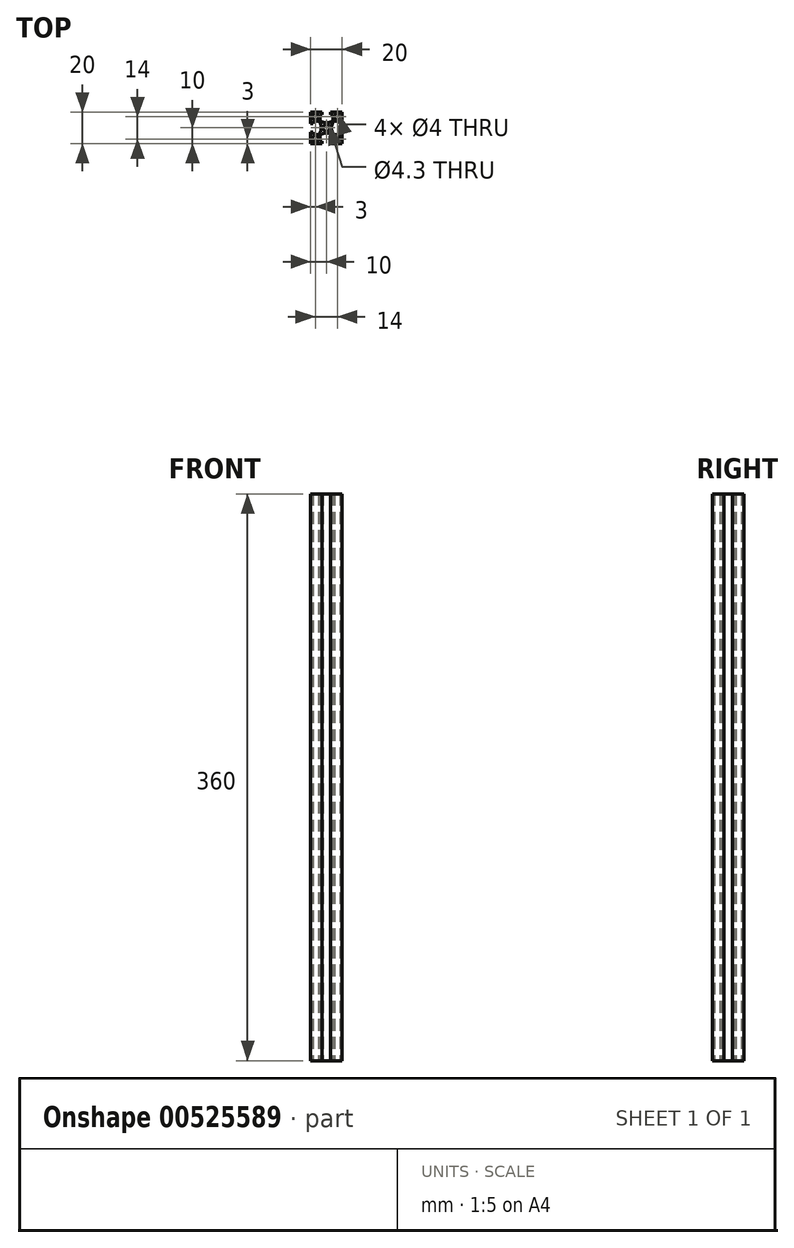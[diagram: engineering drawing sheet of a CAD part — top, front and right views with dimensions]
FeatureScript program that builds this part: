
annotation { "Feature Type Name" : "Feature", "Feature Type Description" : "" }
export const myFeature = defineFeature(function(context is Context, id is Id, definition is map)
    precondition{}
    {
        {
            var Q0;
            Q0=qCreatedBy(makeId("Top.planeOp"),FACE);
            var sketch = newSketch(context, id + "F0", { "sketchPlane" : qUnion([Q0])});
            skCircle(sketch, "E0", {"center": v(-7, 7) * mm, "radius": 2 * mm});
            skCircle(sketch, "E1.MirrorC", {"center": v(-7, -7) * mm, "radius": 2 * mm});
            skLineSegment(sketch, "E2.top", {"start": v(-10, 2.65) * mm, "end": v(-10, -2.65) * mm});
            skLineSegment(sketch, "E2.left", {"start": v(-8.5, 2.65) * mm, "end": v(-10, 2.65) * mm});
            skLineSegment(sketch, "E2.right", {"start": v(-8.5, -2.65) * mm, "end": v(-10, -2.65) * mm});
            skLineSegment(sketch, "E3.bottom", {"start": v(-8.5, 4.15) * mm, "end": v(-8.5, 2.65) * mm});
            skLineSegment(sketch, "E3.left", {"start": v(-8.5, 4.15) * mm, "end": v(-4.55, 4.15) * mm});
            skLineSegment(sketch, "E3.right", {"start": v(-8.5, -4.15) * mm, "end": v(-4.55, -4.15) * mm});
            skArc(sketch, "E4", {"start": v(-4.55, -4.15) * mm, "mid": v(-3.3, 0) * mm, "end": v(-4.55, 4.15) * mm});
            skLineSegment(sketch, "E5.trimOffspring", {"start": v(-8.5, -2.65) * mm, "end": v(-8.5, -4.15) * mm});
            skLineSegment(sketch, "E6.bottom", {"start": v(10, -10) * mm, "end": v(-10, -10) * mm});
            skLineSegment(sketch, "E6.top", {"start": v(10, 10) * mm, "end": v(-10, 10) * mm});
            skLineSegment(sketch, "E6.left", {"start": v(10, -10) * mm, "end": v(10, 10) * mm});
            skLineSegment(sketch, "E6.right", {"start": v(-10, -10) * mm, "end": v(-10, 10) * mm});
            skPoint(sketch, "E6.middle", {"position": v(0, 0) * mm});
            skCircle(sketch, "E7.MirrorC", {"center": v(7, 7) * mm, "radius": 2 * mm});
            skCircle(sketch, "E8.MirrorC", {"center": v(7, -7) * mm, "radius": 2 * mm});
            skLineSegment(sketch, "E9.1.0", {"start": v(-4.15, -8.5) * mm, "end": v(-2.65, -8.5) * mm});
            skArc(sketch, "E9.1.1", {"start": v(4.15, -4.55) * mm, "mid": v(0, -3.3) * mm, "end": v(-4.15, -4.55) * mm});
            skLineSegment(sketch, "E9.1.2", {"start": v(-2.65, -10) * mm, "end": v(2.65, -10) * mm});
            skLineSegment(sketch, "E9.1.3", {"start": v(-2.65, -8.5) * mm, "end": v(-2.65, -10) * mm});
            skLineSegment(sketch, "E9.1.4", {"start": v(-4.15, -8.5) * mm, "end": v(-4.15, -4.55) * mm});
            skLineSegment(sketch, "E9.1.5", {"start": v(2.65, -8.5) * mm, "end": v(4.15, -8.5) * mm});
            skLineSegment(sketch, "E9.1.6", {"start": v(4.15, -8.5) * mm, "end": v(4.15, -4.55) * mm});
            skLineSegment(sketch, "E9.1.7", {"start": v(2.65, -8.5) * mm, "end": v(2.65, -10) * mm});
            skLineSegment(sketch, "E9.2.0", {"start": v(8.5, -4.15) * mm, "end": v(8.5, -2.65) * mm});
            skArc(sketch, "E9.2.1", {"start": v(4.55, 4.15) * mm, "mid": v(3.3, 0) * mm, "end": v(4.55, -4.15) * mm});
            skLineSegment(sketch, "E9.2.2", {"start": v(10, -2.65) * mm, "end": v(10, 2.65) * mm});
            skLineSegment(sketch, "E9.2.3", {"start": v(8.5, -2.65) * mm, "end": v(10, -2.65) * mm});
            skLineSegment(sketch, "E9.2.4", {"start": v(8.5, -4.15) * mm, "end": v(4.55, -4.15) * mm});
            skLineSegment(sketch, "E9.2.5", {"start": v(8.5, 2.65) * mm, "end": v(8.5, 4.15) * mm});
            skLineSegment(sketch, "E9.2.6", {"start": v(8.5, 4.15) * mm, "end": v(4.55, 4.15) * mm});
            skLineSegment(sketch, "E9.2.7", {"start": v(8.5, 2.65) * mm, "end": v(10, 2.65) * mm});
            skLineSegment(sketch, "E9.3.0", {"start": v(4.15, 8.5) * mm, "end": v(2.65, 8.5) * mm});
            skArc(sketch, "E9.3.1", {"start": v(-4.15, 4.55) * mm, "mid": v(0, 3.3) * mm, "end": v(4.15, 4.55) * mm});
            skLineSegment(sketch, "E9.3.2", {"start": v(2.65, 10) * mm, "end": v(-2.65, 10) * mm});
            skLineSegment(sketch, "E9.3.3", {"start": v(2.65, 8.5) * mm, "end": v(2.65, 10) * mm});
            skLineSegment(sketch, "E9.3.4", {"start": v(4.15, 8.5) * mm, "end": v(4.15, 4.55) * mm});
            skLineSegment(sketch, "E9.3.5", {"start": v(-2.65, 8.5) * mm, "end": v(-4.15, 8.5) * mm});
            skLineSegment(sketch, "E9.3.6", {"start": v(-4.15, 8.5) * mm, "end": v(-4.15, 4.55) * mm});
            skLineSegment(sketch, "E9.3.7", {"start": v(-2.65, 8.5) * mm, "end": v(-2.65, 10) * mm});
            skCircle(sketch, "E10", {"center": v(0, 0) * mm, "radius": 2.15 * mm});
            skSolve(sketch);
        }
        {
            var Q0;
            Q0=makeQuery(id+"F0.imprint","IMPRINT",FACE,{"disambiguationData":[TD([[makeQuery(id+"F0.imprint","IMPRINT",EDGE,{"derivedFrom":sQuery(id+"F0.wireOp",EDGE,"E0")}),-1.0]])]});
            extrude(context, id + "F1", {"entities" : qUnion([Q0]), "depth" : 360 * mm, "offsetDistance" : 25 * mm});
        }
    });
